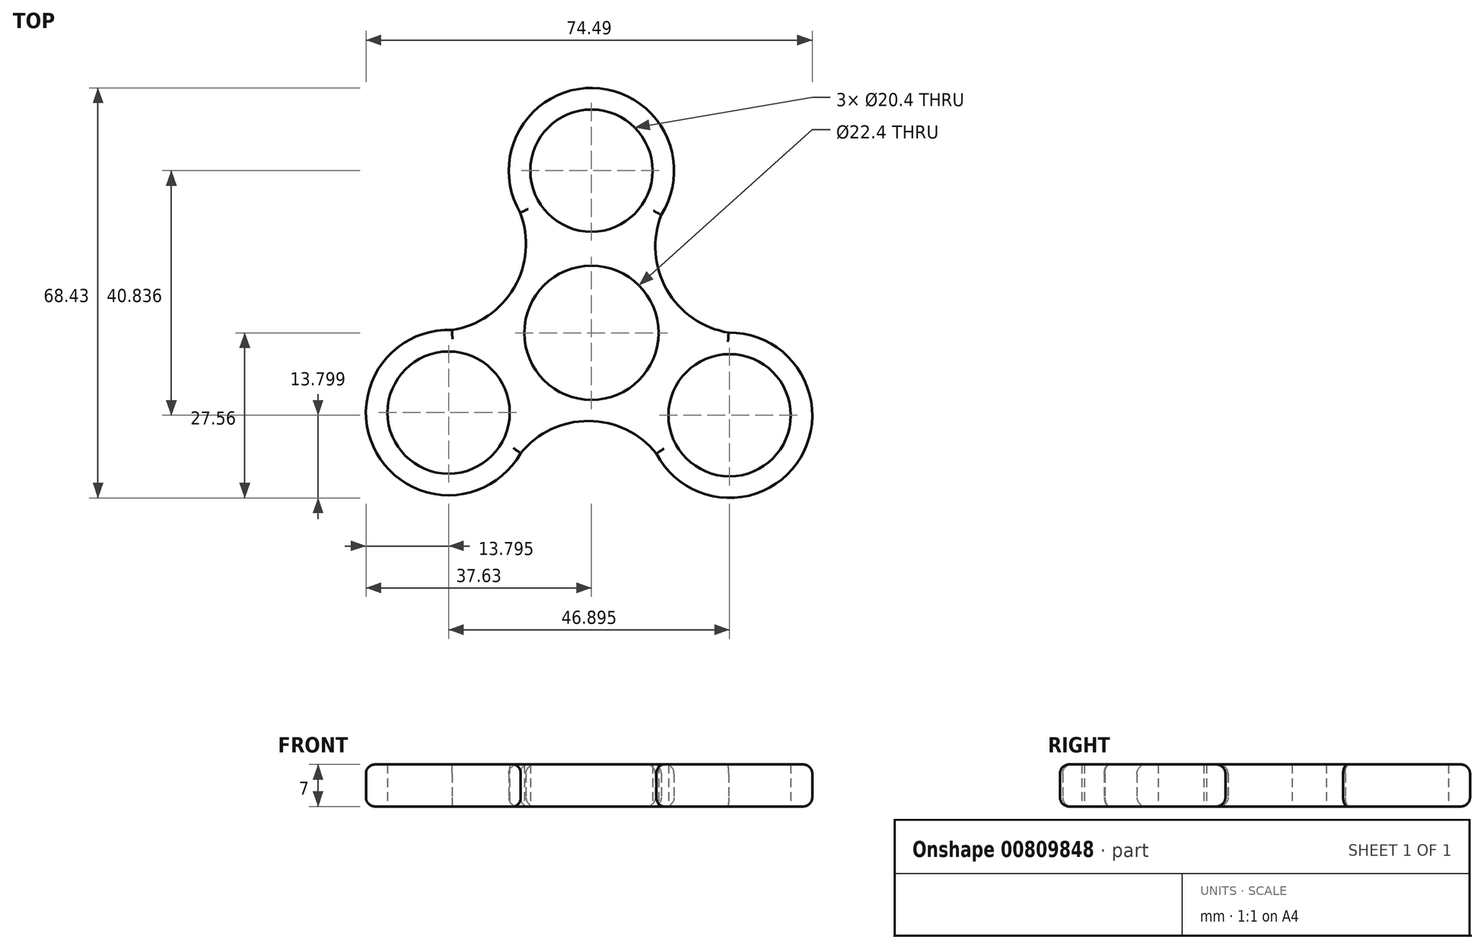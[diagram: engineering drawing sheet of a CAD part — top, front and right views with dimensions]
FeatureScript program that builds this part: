
annotation { "Feature Type Name" : "Feature", "Feature Type Description" : "" }
export const myFeature = defineFeature(function(context is Context, id is Id, definition is map)
    precondition{}
    {
        {
            var Q0;
            Q0=qCreatedBy(makeId("Top.planeOp"),FACE);
            var sketch = newSketch(context, id + "F0", { "sketchPlane" : qUnion([Q0])});
            skCircle(sketch, "E0", {"center": v(0, 0) * mm, "radius": 11.2 * mm});
            skCircle(sketch, "E1", {"center": v(0, 27.07) * mm, "radius": 10.2 * mm});
            skArc(sketch, "E2", {"start": v(11.66, 19.7) * mm, "mid": v(0.2, 40.87) * mm, "end": v(-11.87, 20.04) * mm});
            skArc(sketch, "E3.1.0", {"start": v(-23.27, 0.47) * mm, "mid": v(-35.89, -20.04) * mm, "end": v(-11.8, -20.08) * mm});
            skCircle(sketch, "E3.1.1", {"center": v(-23.83, -13.31) * mm, "radius": 10.2 * mm});
            skArc(sketch, "E3.2.0", {"start": v(10.84, -20.17) * mm, "mid": v(34.9, -20.84) * mm, "end": v(22.9, 0.04) * mm});
            skCircle(sketch, "E3.2.1", {"center": v(23.06, -13.76) * mm, "radius": 10.2 * mm});
            skPoint(sketch, "E3.center", {"position": v(-0.26, 0) * mm});
            skArc(sketch, "E4", {"start": v(12.88, 22.13) * mm, "mid": v(11.97, 8.4) * mm, "end": v(22.9, 0.04) * mm});
            skArc(sketch, "E5.1.0", {"start": v(-26, 0.32) * mm, "mid": v(-13.64, 6.39) * mm, "end": v(-11.87, 20.04) * mm});
            skArc(sketch, "E5.2.0", {"start": v(12.34, -22.45) * mm, "mid": v(0.9, -14.79) * mm, "end": v(-11.8, -20.08) * mm});
            skSolve(sketch);
        }
        {
            var Q0;
            Q0=qSketchRegion(id+"F0",true);
            extrude(context, id + "F1", {"entities" : qUnion([Q0]), "depth" : 7 * mm, "offsetDistance" : 25 * mm});
        }
        {
            var Q0;
            Q0=makeQuery(id+"F1.opExtrude","CAP_EDGE",EDGE,{"disambiguationData":[OSD([sQuery(id+"F0.wireOp",EDGE,"E2")])],"isStart":false});
            var Q1;
            Q1=makeQuery(id+"F1.opExtrude","CAP_EDGE",EDGE,{"disambiguationData":[OSD([sQuery(id+"F0.wireOp",EDGE,"E5.1.0")])],"isStart":false});
            var Q2;
            Q2=makeQuery(id+"F1.opExtrude","CAP_EDGE",EDGE,{"disambiguationData":[OSD([sQuery(id+"F0.wireOp",EDGE,"E3.1.0")])],"isStart":false});
            var Q3;
            Q3=makeQuery(id+"F1.opExtrude","CAP_EDGE",EDGE,{"disambiguationData":[OSD([sQuery(id+"F0.wireOp",EDGE,"E5.2.0")])],"isStart":false});
            var Q4;
            Q4=makeQuery(id+"F1.opExtrude","CAP_EDGE",EDGE,{"disambiguationData":[OSD([sQuery(id+"F0.wireOp",EDGE,"E3.2.0")])],"isStart":false});
            var Q5;
            Q5=makeQuery(id+"F1.opExtrude","CAP_EDGE",EDGE,{"disambiguationData":[OSD([sQuery(id+"F0.wireOp",EDGE,"E4")])],"isStart":false});
            var Q6;
            Q6=makeQuery(id+"F1.opExtrude","CAP_EDGE",EDGE,{"disambiguationData":[OSD([sQuery(id+"F0.wireOp",EDGE,"E2")])],"isStart":true});
            var Q7;
            Q7=makeQuery(id+"F1.opExtrude","CAP_EDGE",EDGE,{"disambiguationData":[OSD([sQuery(id+"F0.wireOp",EDGE,"E5.1.0")])],"isStart":true});
            var Q8;
            Q8=makeQuery(id+"F1.opExtrude","CAP_EDGE",EDGE,{"disambiguationData":[OSD([sQuery(id+"F0.wireOp",EDGE,"E3.1.0")])],"isStart":true});
            var Q9;
            Q9=makeQuery(id+"F1.opExtrude","CAP_EDGE",EDGE,{"disambiguationData":[OSD([sQuery(id+"F0.wireOp",EDGE,"E5.2.0")])],"isStart":true});
            var Q10;
            Q10=makeQuery(id+"F1.opExtrude","CAP_EDGE",EDGE,{"disambiguationData":[OSD([sQuery(id+"F0.wireOp",EDGE,"E3.2.0")])],"isStart":true});
            var Q11;
            Q11=makeQuery(id+"F1.opExtrude","CAP_EDGE",EDGE,{"disambiguationData":[OSD([sQuery(id+"F0.wireOp",EDGE,"E4")])],"isStart":true});
            fillet(context, id + "F2", {"entities" : qUnion([Q0, Q1, Q2, Q3, Q4, Q5, Q6, Q7, Q8, Q9, Q10, Q11]), "radius" : 1.5 * mm, "tangentPropagation" : true, "allowEdgeOverflow" : false});
        }
    });
